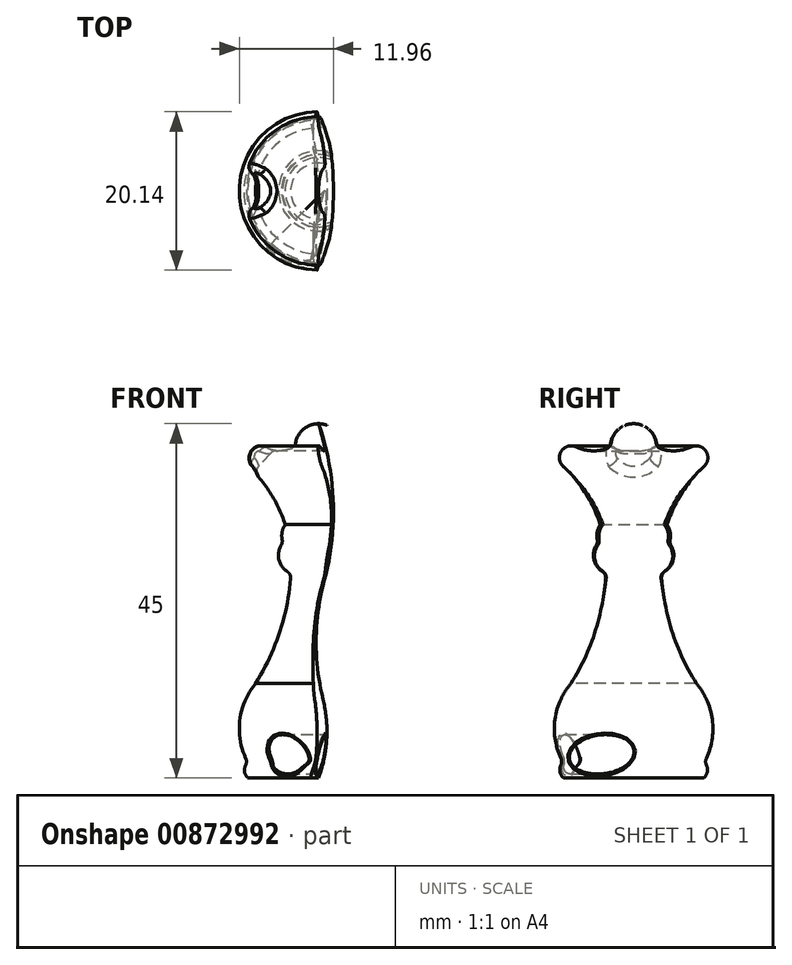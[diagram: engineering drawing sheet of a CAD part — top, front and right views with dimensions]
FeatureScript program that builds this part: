
annotation { "Feature Type Name" : "Feature", "Feature Type Description" : "" }
export const myFeature = defineFeature(function(context is Context, id is Id, definition is map)
    precondition{}
    {
        {
            var Q0;
            Q0=qCreatedBy(makeId("Front.planeOp"),FACE);
            var sketch = newSketch(context, id + "F0", { "sketchPlane" : qUnion([Q0])});
            skLineSegment(sketch, "E0", {"start": v(0, 50) * mm, "end": v(0, 0) * mm, "construction": true});
            skArc(sketch, "E1", {"start": v(9, 0) * mm, "mid": v(9.41, 1) * mm, "end": v(9, 2) * mm});
            skLineSegment(sketch, "E2", {"start": v(9, 0) * mm, "end": v(11.06, 2.06) * mm, "construction": true});
            skArc(sketch, "E3", {"start": v(9, 2) * mm, "mid": v(10.03, 7.15) * mm, "end": v(8, 12) * mm});
            skArc(sketch, "E4", {"start": v(3.5, 26) * mm, "mid": v(4.88, 18.72) * mm, "end": v(8, 12) * mm});
            skArc(sketch, "E5", {"start": v(8.95, 39.58) * mm, "mid": v(9.18, 41.53) * mm, "end": v(7.29, 42.04) * mm});
            skArc(sketch, "E6", {"start": v(2.96, 42.04) * mm, "mid": v(5.12, 41.55) * mm, "end": v(7.29, 42.04) * mm});
            skArc(sketch, "E7", {"start": v(2.96, 42.04) * mm, "mid": v(2.1, 44.13) * mm, "end": v(0, 45) * mm});
            skLineSegment(sketch, "E8", {"start": v(0, 45) * mm, "end": v(6.97, 45) * mm, "construction": true});
            skArc(sketch, "E9", {"start": v(8.95, 39.58) * mm, "mid": v(4.69, 33.4) * mm, "end": v(3.5, 26) * mm});
            skLineSegment(sketch, "E10", {"start": v(0, 45) * mm, "end": v(0, 0) * mm});
            skLineSegment(sketch, "E11", {"start": v(9, 0) * mm, "end": v(0, 0) * mm});
            skLineSegment(sketch, "E12", {"start": v(0, 42.04) * mm, "end": v(2.96, 42.04) * mm, "construction": true});
            skLineSegment(sketch, "E13", {"start": v(7.29, 42.04) * mm, "end": v(7.94, 40.69) * mm, "construction": true});
            skLineSegment(sketch, "E14", {"start": v(7.94, 40.69) * mm, "end": v(8.95, 39.58) * mm, "construction": true});
            skSolve(sketch);
        }
        {
            var Q0;
            Q0 = qSketchRegion(id + "F0", true);
            var Q1;
            Q1=sQuery(id+"F0.wireOp",EDGE,"E10");
            revolve(context, id + "F1", {"surfaceOperationType" : NewSurfaceOperationType.NEW, "entities" : qUnion([Q0]), "axis" : qUnion([Q1]), "revolveType" : RevolveType.FULL});
        }
        {
            var Q0;
            Q0=qCreatedBy(makeId("Front.planeOp"),FACE);
            var sketch = newSketch(context, id + "F2", { "sketchPlane" : qUnion([Q0])});
            skArc(sketch, "E15", {"start": v(-8.95, 39.58) * mm, "mid": v(-4.69, 33.4) * mm, "end": v(-3.5, 26) * mm, "construction": true});
            skArc(sketch, "E16", {"start": v(3.5, 26) * mm, "mid": v(4.69, 33.4) * mm, "end": v(8.95, 39.58) * mm, "construction": true});
            skArc(sketch, "E17", {"start": v(-3.5, 26) * mm, "mid": v(-4.88, 18.72) * mm, "end": v(-8, 12) * mm, "construction": true});
            skArc(sketch, "E18", {"start": v(8, 12) * mm, "mid": v(4.88, 18.72) * mm, "end": v(3.5, 26) * mm, "construction": true});
            skArc(sketch, "E19", {"start": v(-3.5, 26) * mm, "mid": v(-3.59, 29.12) * mm, "end": v(-4.25, 32.17) * mm});
            skLineSegment(sketch, "E20", {"start": v(0, -0.88) * mm, "end": v(0, 52.26) * mm});
            skLineSegment(sketch, "E21", {"start": v(-3.5, 26) * mm, "end": v(-9.07, 28.03) * mm, "construction": true});
            skLineSegment(sketch, "E22", {"start": v(-3.5, 26) * mm, "end": v(-13.81, 26) * mm, "construction": true});
            skArc(sketch, "E23", {"start": v(-4.25, 32.17) * mm, "mid": v(-4.66, 31.06) * mm, "end": v(-4.52, 29.88) * mm});
            skArc(sketch, "E24", {"start": v(-4.52, 29.88) * mm, "mid": v(-5.02, 27.67) * mm, "end": v(-3.5, 26) * mm});
            skSolve(sketch);
        }
        {
            var Q0;
            Q0 = qSketchRegion(id + "F2", true);
            var Q1;
            Q1=sQuery(id+"F2.wireOp",EDGE,"E20");
            revolve(context, id + "F3", {"operationType" : NewBodyOperationType.ADD, "surfaceOperationType" : NewSurfaceOperationType.NEW, "entities" : qUnion([Q0]), "axis" : qUnion([Q1]), "revolveType" : RevolveType.FULL});
        }
        {
            var Q0;
            Q0=qCreatedBy(makeId("Front.planeOp"),FACE);
            var sketch = newSketch(context, id + "F4", { "sketchPlane" : qUnion([Q0])});
            skArc(sketch, "E25", {"start": v(-8.95, 39.58) * mm, "mid": v(-9.18, 41.53) * mm, "end": v(-7.29, 42.04) * mm});
            skArc(sketch, "E26", {"start": v(7.29, 42.04) * mm, "mid": v(9.18, 41.53) * mm, "end": v(8.95, 39.58) * mm});
            skArc(sketch, "E27", {"start": v(-8.95, 39.58) * mm, "mid": v(-6.11, 36.19) * mm, "end": v(-4.25, 32.17) * mm});
            skArc(sketch, "E28", {"start": v(4.25, 32.17) * mm, "mid": v(6.11, 36.19) * mm, "end": v(8.95, 39.58) * mm});
            skLineSegment(sketch, "E29", {"start": v(-8.95, 39.58) * mm, "end": v(-15.96, 31.97) * mm});
            skLineSegment(sketch, "E30", {"start": v(-8.95, 39.58) * mm, "end": v(-15.8, 45.9) * mm});
            skSolve(sketch);
        }
        {
            var Q0;
            Q0=sQuery(id+"F4.wireOp",VERTEX,"E25.start");
            var Q1;
            Q1=sQuery(id+"F4.wireOp",EDGE,"E29");
            cPlane(context, id + "F5", {"entities" : qUnion([Q0, Q1]), "cplaneType" : CPlaneType.LINE_POINT, "offset" : 25 * mm, "width" : 150 * mm, "height" : 150 * mm});
        }
        {
            var Q0;
            Q0=qCreatedBy(id+"F5.planeOp",FACE);
            var sketch = newSketch(context, id + "F6", { "sketchPlane" : qUnion([Q0])});
            skCircle(sketch, "E31", {"center": v(-34.9, 0) * mm, "radius": 2.5 * mm});
            skLineSegment(sketch, "E32", {"start": v(-4.94, 0) * mm, "end": v(-34.9, 0) * mm});
            skFitSpline(sketch, "E33", {"points": [v(-31.24, -8.24) * mm, v(-32.4, -7.2) * mm, v(-33.42, -5.8) * mm, v(-34.22, -4.13) * mm, v(-34.75, -2.24) * mm, v(-34.95, -0.22) * mm, v(-34.82, 1.8) * mm, v(-34.36, 3.73) * mm, v(-33.62, 5.46) * mm, v(-32.64, 6.92) * mm, v(-31.5, 8.04) * mm, v(-30.27, 8.83) * mm, v(-29, 9.3) * mm, v(-27.7, 9.48) * mm, v(-26.4, 9.37) * mm, v(-25.12, 8.96) * mm, v(-23.88, 8.24) * mm, v(-22.71, 7.2) * mm, v(-21.7, 5.8) * mm, v(-20.9, 4.13) * mm, v(-20.37, 2.24) * mm, v(-20.17, 0.22) * mm, v(-20.3, -1.8) * mm, v(-20.75, -3.73) * mm, v(-21.5, -5.46) * mm, v(-22.47, -6.92) * mm, v(-23.61, -8.04) * mm, v(-24.84, -8.83) * mm, v(-26.12, -9.3) * mm, v(-27.42, -9.48) * mm, v(-28.71, -9.37) * mm, v(-30, -8.96) * mm, v(-31.24, -8.24) * mm, v(-32.4, -7.2) * mm, v(-33.42, -5.8) * mm, v(-31.24, -8.24) * mm]});
            skSolve(sketch);
        }
        {
            var Q0;
            {var subQ0=sQuery(id+"F6.wireOp",EDGE,"E33");var subQ1=sQuery(id+"F6.wireOp",EDGE,"E31");var subQ2=makeQuery(id+"F6.imprint","INTERSECT",VERTEX,{"disambiguationData":[OD(0.0)],"derivedFrom":[subQ1,subQ0]});Q0=makeQuery(id+"F6.imprint","IMPRINT",FACE,{"disambiguationData":[TD([[makeQuery(id+"F6.imprint","IMPRINT",EDGE,{"disambiguationData":[TD([[subQ2,-1.0]])],"derivedFrom":subQ1}),1.0]])]});}
            var Q1;
            {var subQ0=sQuery(id+"F6.wireOp",EDGE,"E33");var subQ1=sQuery(id+"F6.wireOp",EDGE,"E31");var subQ2=makeQuery(id+"F6.imprint","INTERSECT",VERTEX,{"disambiguationData":[OD(1.0)],"derivedFrom":[subQ1,subQ0]});Q1=makeQuery(id+"F6.imprint","IMPRINT",FACE,{"disambiguationData":[TD([[makeQuery(id+"F6.imprint","IMPRINT",EDGE,{"disambiguationData":[TD([[subQ2,-1.0]])],"derivedFrom":subQ1}),1.0]])]});}
            var Q2;
            {var subQ0=sQuery(id+"F6.wireOp",EDGE,"E33");var subQ1=sQuery(id+"F6.wireOp",EDGE,"E31");var subQ2=makeQuery(id+"F6.imprint","INTERSECT",VERTEX,{"disambiguationData":[OD(0.0)],"derivedFrom":[subQ1,subQ0]});Q2=makeQuery(id+"F6.imprint","IMPRINT",FACE,{"disambiguationData":[TD([[makeQuery(id+"F6.imprint","IMPRINT",EDGE,{"disambiguationData":[TD([[subQ2,1.0]])],"derivedFrom":subQ1}),1.0]])]});}
            extrude(context, id + "F7", {"entities" : qUnion([Q0, Q1, Q2]), "operationType" : NewBodyOperationType.REMOVE, "oppositeDirection" : true, "depth" : 5.8 * mm, "offsetDistance" : 25 * mm, "hasSecondDirection" : true, "secondDirectionOppositeDirection" : false, "secondDirectionDepth" : 25 * mm});
        }
        {
            var Q0;
            Q0=makeQuery(id+"F7.boolean.opBoolean","INTERSECT",EDGE,{"disambiguationData":[OD(0.0)],"derivedFrom":[makeQuery(id+"F1.opRevolve","SWEPT_FACE",FACE,{"disambiguationData":[OSD([sQuery(id+"F0.wireOp",EDGE,"E5")])]}),makeQuery(id+"F7.opExtrude","SWEPT_FACE",FACE,{"disambiguationData":[OSD([sQuery(id+"F6.wireOp",EDGE,"E31")])]})]});
            fillet(context, id + "F8", {"entities" : qUnion([Q0]), "radius" : 1 * mm, "tangentPropagation" : true, "allowEdgeOverflow" : false});
        }
        {
            var Q0;
            Q0=makeQuery(id+"F1.opRevolve","SWEPT_EDGE",EDGE,{"disambiguationData":[OSD([sQuery(id+"F0.wireOp",EDGE,"E6"),sQuery(id+"F0.wireOp",EDGE,"E7")])]});
            fillet(context, id + "F9", {"entities" : qUnion([Q0]), "radius" : 1 * mm, "tangentPropagation" : true, "allowEdgeOverflow" : false});
        }
        {
            var Q0;
            Q0=makeQuery(id+"F3.opRevolve","SWEPT_EDGE",EDGE,{"disambiguationData":[OSD([sQuery(id+"F2.wireOp",EDGE,"E19"),sQuery(id+"F2.wireOp",EDGE,"E23")])]});
            var Q1;
            Q1=makeQuery(id+"F3.boolean.opBoolean","MERGE",EDGE,{"derivedFrom":[makeQuery(id+"F1.opRevolve","SWEPT_EDGE",EDGE,{"disambiguationData":[OSD([sQuery(id+"F0.wireOp",EDGE,"E4"),sQuery(id+"F0.wireOp",EDGE,"E9")])]}),makeQuery(id+"F3.opRevolve","SWEPT_EDGE",EDGE,{"disambiguationData":[OSD([sQuery(id+"F2.wireOp",EDGE,"E19"),sQuery(id+"F2.wireOp",EDGE,"E24")])]})]});
            var Q2;
            Q2=makeQuery(id+"F3.opRevolve","SWEPT_EDGE",EDGE,{"disambiguationData":[OSD([sQuery(id+"F2.wireOp",EDGE,"E23"),sQuery(id+"F2.wireOp",EDGE,"E24")])]});
            var Q3;
            Q3=makeQuery(id+"F1.opRevolve","SWEPT_EDGE",EDGE,{"disambiguationData":[OSD([sQuery(id+"F0.wireOp",EDGE,"E1"),sQuery(id+"F0.wireOp",EDGE,"E3")])]});
            fillet(context, id + "F10", {"entities" : qUnion([Q0, Q1, Q2, Q3]), "radius" : 1 * mm, "tangentPropagation" : true, "allowEdgeOverflow" : false});
        }
        {
            var Q0;
            Q0=qCreatedBy(makeId("Front.planeOp"),FACE);
            var sketch = newSketch(context, id + "F11", { "sketchPlane" : qUnion([Q0])});
            skArc(sketch, "E34", {"start": v(0.72, 25) * mm, "mid": v(1.86, 35.05) * mm, "end": v(0, 45) * mm});
            skArc(sketch, "E35", {"start": v(0.72, 25) * mm, "mid": v(-0.31, 17.5) * mm, "end": v(0.57, 10) * mm});
            skArc(sketch, "E36", {"start": v(0, 0) * mm, "mid": v(1.04, 4.96) * mm, "end": v(0.57, 10) * mm});
            skArc(sketch, "E37", {"start": v(-2.91, 42.56) * mm, "mid": v(0, 45) * mm, "end": v(2.91, 42.56) * mm, "construction": true});
            skLineSegment(sketch, "E38", {"start": v(0, 0) * mm, "end": v(-40, 0) * mm});
            skLineSegment(sketch, "E39", {"start": v(-40, 0) * mm, "end": v(-40, 45) * mm});
            skLineSegment(sketch, "E40", {"start": v(-40, 45) * mm, "end": v(0, 45) * mm});
            skSolve(sketch);
        }
        {
            var Q0;
            Q0 = qSketchRegion(id + "F11", true);
            var Q1;
            Q1=sQuery(id+"F11.wireOp",EDGE,"E39");
            revolve(context, id + "F12", {"surfaceOperationType" : NewSurfaceOperationType.NEW, "entities" : qUnion([Q0]), "axis" : qUnion([Q1]), "revolveType" : RevolveType.FULL});
        }
        {
            var Q0;
            Q0=makeQuery(id+"F1.opRevolve","SWEPT_BODY",BODY,{"disambiguationData":[OSD([sQuery(id+"F0.wireOp",EDGE,"E1"),sQuery(id+"F0.wireOp",EDGE,"E3"),sQuery(id+"F0.wireOp",EDGE,"E4"),sQuery(id+"F0.wireOp",EDGE,"E5"),sQuery(id+"F0.wireOp",EDGE,"E6"),sQuery(id+"F0.wireOp",EDGE,"E7"),sQuery(id+"F0.wireOp",EDGE,"E9"),sQuery(id+"F0.wireOp",EDGE,"E10"),sQuery(id+"F0.wireOp",EDGE,"E11")])]});
            var Q1;
            Q1=makeQuery(id+"F12.opRevolve","SWEPT_BODY",BODY,{"disambiguationData":[OSD([sQuery(id+"F11.wireOp",EDGE,"E34"),sQuery(id+"F11.wireOp",EDGE,"E35"),sQuery(id+"F11.wireOp",EDGE,"E36"),sQuery(id+"F11.wireOp",EDGE,"E38"),sQuery(id+"F11.wireOp",EDGE,"E39"),sQuery(id+"F11.wireOp",EDGE,"E40")])]});
            booleanBodies(context, id + "F13", {"operationType" : BooleanOperationType.INTERSECTION, "tools" : qUnion([Q0, Q1])});
        }
        {
            var Q0;
            Q0=qCreatedBy(makeId("Top.planeOp"),FACE);
            var sketch = newSketch(context, id + "F14", { "sketchPlane" : qUnion([Q0])});
            skLineSegment(sketch, "E41", {"start": v(0, -5) * mm, "end": v(5.25, 0.25) * mm});
            skSolve(sketch);
        }
        {
            var Q0;
            Q0=sQuery(id+"F14.wireOp",VERTEX,"E41.start");
            var Q1;
            Q1=sQuery(id+"F14.wireOp",EDGE,"E41");
            cPlane(context, id + "F15", {"entities" : qUnion([Q0, Q1]), "cplaneType" : CPlaneType.LINE_POINT, "offset" : 25 * mm, "width" : 150 * mm, "height" : 150 * mm});
        }
        {
            var Q0;
            Q0=qCreatedBy(id+"F15.planeOp",FACE);
            var sketch = newSketch(context, id + "F16", { "sketchPlane" : qUnion([Q0])});
            skCircle(sketch, "E42", {"center": v(-3, 3) * mm, "radius": 2.5 * mm});
            skSolve(sketch);
        }
        {
            var Q0;
            Q0 = qSketchRegion(id + "F16", true);
            extrude(context, id + "F17", {"entities" : qUnion([Q0]), "operationType" : NewBodyOperationType.REMOVE, "oppositeDirection" : true, "depth" : 25 * mm, "offsetDistance" : 25 * mm, "hasSecondDirection" : true, "secondDirectionOppositeDirection" : false, "secondDirectionDepth" : 25 * mm});
        }
        {
            var Q0;
            Q0=makeQuery(id+"F17.boolean.opBoolean","INTERSECT",EDGE,{"derivedFrom":[makeQuery(id+"F1.opRevolve","SWEPT_FACE",FACE,{"disambiguationData":[OSD([sQuery(id+"F0.wireOp",EDGE,"E3")])]}),makeQuery(id+"F17.opExtrude","SWEPT_FACE",FACE,{"disambiguationData":[OSD([sQuery(id+"F16.wireOp",EDGE,"E42")])]})]});
            var Q1;
            Q1=makeQuery(id+"F17.boolean.opBoolean","INTERSECT",EDGE,{"derivedFrom":[makeQuery(id+"F12.opRevolve","SWEPT_FACE",FACE,{"disambiguationData":[OSD([sQuery(id+"F11.wireOp",EDGE,"E36")])]}),makeQuery(id+"F17.opExtrude","SWEPT_FACE",FACE,{"disambiguationData":[OSD([sQuery(id+"F16.wireOp",EDGE,"E42")])]})]});
            var Q2;
            Q2=makeQuery(id+"F17.boolean.opBoolean","INTERSECT",EDGE,{"derivedFrom":[makeQuery(id+"F1.opRevolve","SWEPT_FACE",FACE,{"disambiguationData":[OSD([sQuery(id+"F0.wireOp",EDGE,"E1")])]}),makeQuery(id+"F17.opExtrude","SWEPT_FACE",FACE,{"disambiguationData":[OSD([sQuery(id+"F16.wireOp",EDGE,"E42")])]})]});
            var Q3;
            Q3=makeQuery(id+"F17.boolean.opBoolean","INTERSECT",EDGE,{"disambiguationData":[OD(0.0)],"derivedFrom":[makeQuery(id+"F10.opFillet","BLEND_FACE",FACE,{"disambiguationData":[OSD([sQuery(id+"F0.wireOp",EDGE,"E1"),sQuery(id+"F0.wireOp",EDGE,"E3")])]}),makeQuery(id+"F17.opExtrude","SWEPT_FACE",FACE,{"disambiguationData":[OSD([sQuery(id+"F16.wireOp",EDGE,"E42")])]})]});
            var Q4;
            Q4=makeQuery(id+"F17.boolean.opBoolean","INTERSECT",EDGE,{"disambiguationData":[OD(1.0)],"derivedFrom":[makeQuery(id+"F10.opFillet","BLEND_FACE",FACE,{"disambiguationData":[OSD([sQuery(id+"F0.wireOp",EDGE,"E1"),sQuery(id+"F0.wireOp",EDGE,"E3")])]}),makeQuery(id+"F17.opExtrude","SWEPT_FACE",FACE,{"disambiguationData":[OSD([sQuery(id+"F16.wireOp",EDGE,"E42")])]})]});
            fillet(context, id + "F18", {"entities" : qUnion([Q0, Q1, Q2, Q3, Q4]), "radius" : 0.2 * mm, "tangentPropagation" : true, "allowEdgeOverflow" : false});
        }
    });
